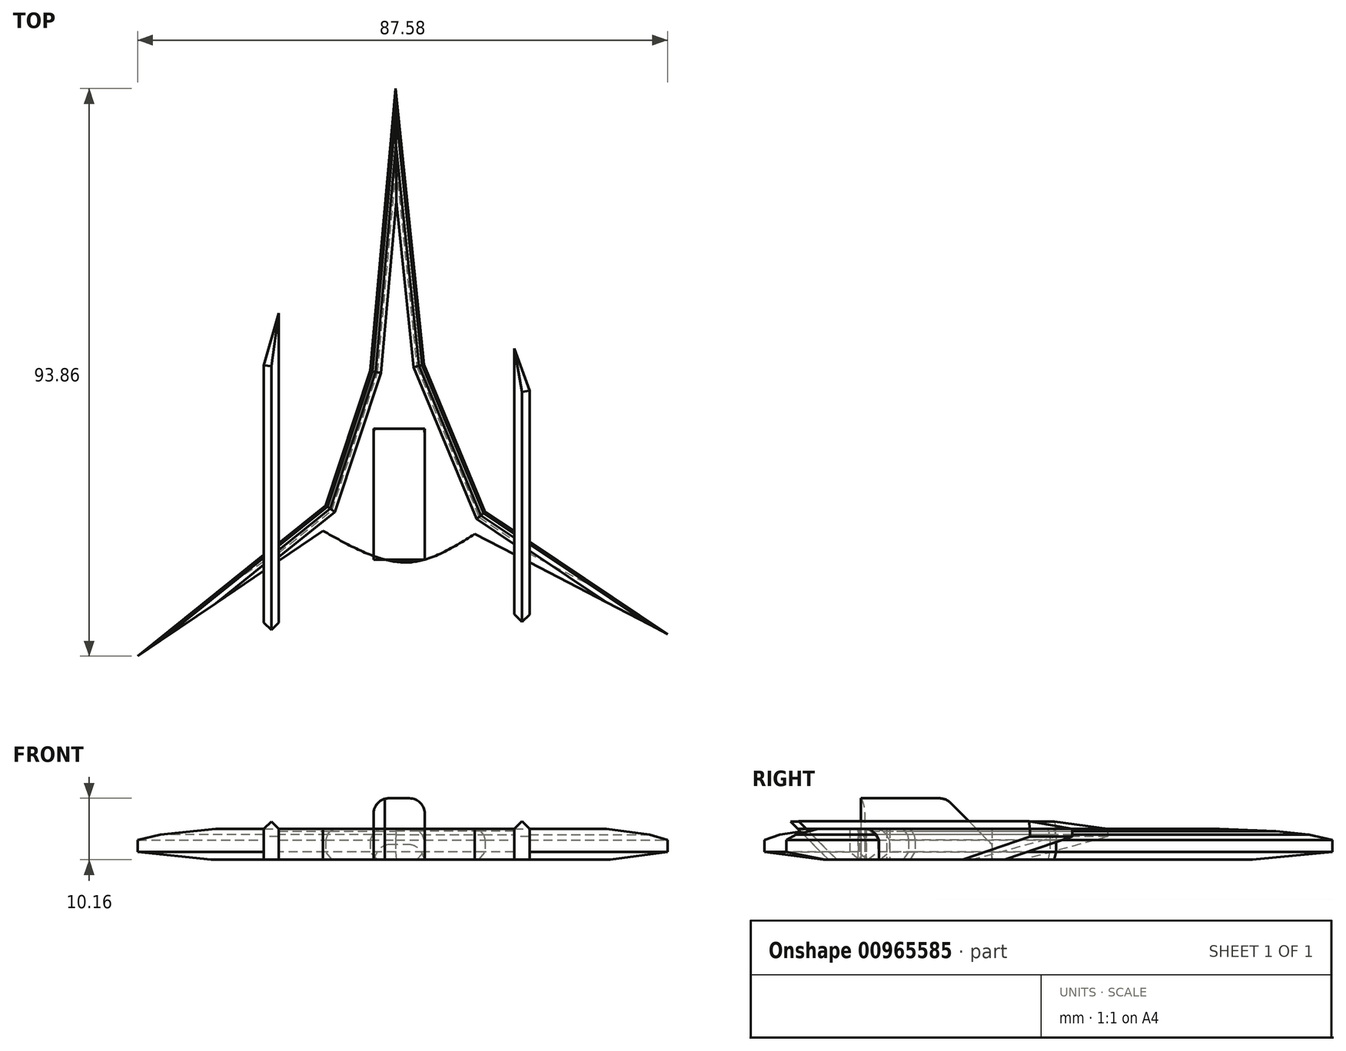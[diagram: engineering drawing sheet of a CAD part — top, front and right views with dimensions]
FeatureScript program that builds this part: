
annotation { "Feature Type Name" : "Feature", "Feature Type Description" : "" }
export const myFeature = defineFeature(function(context is Context, id is Id, definition is map)
    precondition{}
    {
        {
            var Q0;
            Q0=qCreatedBy(makeId("Top.planeOp"),FACE);
            var sketch = newSketch(context, id + "F0", { "sketchPlane" : qUnion([Q0])});
            skLineSegment(sketch, "E0", {"start": v(-29.34, 58.5) * mm, "end": v(-24.64, 12.89) * mm});
            skLineSegment(sketch, "E1", {"start": v(-29.34, 58.5) * mm, "end": v(-33.57, 11.83) * mm});
            skLineSegment(sketch, "E2", {"start": v(-33.57, 11.83) * mm, "end": v(-42.08, -13.88) * mm});
            skLineSegment(sketch, "E3", {"start": v(-24.64, 12.89) * mm, "end": v(-14.54, -11.5) * mm});
            skLineSegment(sketch, "E4", {"start": v(-40.93, -10.42) * mm, "end": v(-72, -35.35) * mm});
            skLineSegment(sketch, "E5", {"start": v(-14.54, -11.5) * mm, "end": v(15.58, -31.7) * mm});
            skLineSegment(sketch, "E6", {"start": v(-72, -35.35) * mm, "end": v(-41.35, -14.63) * mm});
            skLineSegment(sketch, "E7", {"start": v(15.58, -31.7) * mm, "end": v(-16.28, -15.15) * mm});
            skFitSpline(sketch, "E8", {"points": [v(-16.28, -15.15) * mm, v(-27.6, -19.85) * mm, v(-41.35, -14.63) * mm], "startDerivative": vector(-23.1, -14.59) * mm, "endDerivative": vector(-26.99, 15.18) * mm});
            skLineSegment(sketch, "E9.bottom", {"start": v(-33, 2.26) * mm, "end": v(-24.55, 2.26) * mm});
            skLineSegment(sketch, "E9.top", {"start": v(-33, -19.38) * mm, "end": v(-24.55, -19.38) * mm});
            skLineSegment(sketch, "E9.left", {"start": v(-33, 2.26) * mm, "end": v(-33, -19.38) * mm});
            skLineSegment(sketch, "E9.right", {"start": v(-24.55, 2.26) * mm, "end": v(-24.55, -19.38) * mm});
            skLineSegment(sketch, "E10", {"start": v(-51.12, 12.75) * mm, "end": v(-51.12, -32.34) * mm});
            skLineSegment(sketch, "E11", {"start": v(-51.12, -32.34) * mm, "end": v(-48.68, -32.36) * mm});
            skLineSegment(sketch, "E12", {"start": v(-48.68, -32.36) * mm, "end": v(-48.68, 21.35) * mm});
            skLineSegment(sketch, "E13", {"start": v(-48.68, 21.35) * mm, "end": v(-51.12, 12.75) * mm});
            skLineSegment(sketch, "E14", {"start": v(-9.77, 15.52) * mm, "end": v(-9.77, -30.95) * mm});
            skLineSegment(sketch, "E15", {"start": v(-7.24, -30.98) * mm, "end": v(-7.24, 8.56) * mm});
            skLineSegment(sketch, "E16", {"start": v(-7.24, 8.56) * mm, "end": v(-9.77, 15.52) * mm});
            skLineSegment(sketch, "E17", {"start": v(-7.24, -30.98) * mm, "end": v(-9.77, -30.95) * mm});
            skSolve(sketch);
        }
        {
            var Q0;
            Q0=makeQuery(id+"F0.imprint","IMPRINT",FACE,{"disambiguationData":[TD([[makeQuery(id+"F0.imprint","IMPRINT",EDGE,{"derivedFrom":sQuery(id+"F0.wireOp",EDGE,"E0")}),-1.0]])]});
            var Q1;
            {var subQ0=sQuery(id+"F0.wireOp",EDGE,"E9.top");var subQ1=sQuery(id+"F0.wireOp",EDGE,"E8");var subQ3=makeQuery(id+"F0.imprint","INTERSECT",VERTEX,{"derivedFrom":[subQ1,subQ0]});Q1=makeQuery(id+"F0.imprint","IMPRINT",FACE,{"disambiguationData":[TD([[makeQuery(id+"F0.imprint","IMPRINT",EDGE,{"disambiguationData":[TD([[subQ3,1.0]])],"derivedFrom":subQ1}),-1.0]])]});}
            var Q2;
            {var subQ0=sQuery(id+"F0.wireOp",EDGE,"E9.top");var subQ1=sQuery(id+"F0.wireOp",EDGE,"E8");var subQ2=makeQuery(id+"F0.imprint","INTERSECT",VERTEX,{"derivedFrom":[subQ1,subQ0]});Q2=makeQuery(id+"F0.imprint","IMPRINT",FACE,{"disambiguationData":[TD([[makeQuery(id+"F0.imprint","IMPRINT",EDGE,{"disambiguationData":[TD([[subQ2,-1.0]])],"derivedFrom":subQ1}),1.0]])]});}
            var Q3;
            {var subQ0=sQuery(id+"F0.wireOp",EDGE,"E6");var subQ1=sQuery(id+"F0.wireOp",EDGE,"E4");var subQ2=makeQuery(id+"F0.imprint","INTERSECT",VERTEX,{"derivedFrom":[subQ1,subQ0]});Q3=makeQuery(id+"F0.imprint","IMPRINT",FACE,{"disambiguationData":[TD([[makeQuery(id+"F0.imprint","IMPRINT",EDGE,{"disambiguationData":[TD([[subQ2,1.0]])],"derivedFrom":subQ1}),1.0]])]});}
            var Q4;
            {var subQ0=sQuery(id+"F0.wireOp",EDGE,"E7");var subQ1=sQuery(id+"F0.wireOp",EDGE,"E5");var subQ2=makeQuery(id+"F0.imprint","INTERSECT",VERTEX,{"derivedFrom":[subQ1,subQ0]});Q4=makeQuery(id+"F0.imprint","IMPRINT",FACE,{"disambiguationData":[TD([[makeQuery(id+"F0.imprint","IMPRINT",EDGE,{"disambiguationData":[TD([[subQ2,1.0]])],"derivedFrom":subQ1}),-1.0]])]});}
            extrude(context, id + "F1", {"entities" : qUnion([Q0, Q1, Q2, Q3, Q4]), "depth" : 5.08 * mm, "offsetDistance" : 25.4 * mm});
        }
        {
            var Q0;
            Q0=makeQuery(id+"F1.opExtrude","CAP_EDGE",EDGE,{"disambiguationData":[OSD([sQuery(id+"F0.wireOp",EDGE,"E0")])],"isStart":false});
            var Q1;
            Q1=makeQuery(id+"F1.opExtrude","CAP_EDGE",EDGE,{"disambiguationData":[OSD([sQuery(id+"F0.wireOp",EDGE,"E1")])],"isStart":false});
            var Q2;
            Q2=makeQuery(id+"F1.opExtrude","CAP_EDGE",EDGE,{"disambiguationData":[OSD([sQuery(id+"F0.wireOp",EDGE,"E2")])],"isStart":false});
            var Q3;
            Q3=makeQuery(id+"F1.opExtrude","CAP_EDGE",EDGE,{"disambiguationData":[OSD([sQuery(id+"F0.wireOp",EDGE,"E3")])],"isStart":false});
            var Q4;
            {var subQ0=sQuery(id+"F0.wireOp",EDGE,"E4");Q4=makeQuery(id+"F1.opExtrude","CAP_EDGE",EDGE,{"disambiguationData":[OSD([subQ0]),TDD([makeQuery(id+"F0.imprint","IMPRINT",EDGE,{"disambiguationData":[TD([[makeQuery(id+"F0.imprint","INTERSECT",VERTEX,{"derivedFrom":[subQ0,sQuery(id+"F0.wireOp",EDGE,"E6")]}),1.0]])],"derivedFrom":subQ0})])],"isStart":false});}
            var Q5;
            {var subQ0=sQuery(id+"F0.wireOp",EDGE,"E5");Q5=makeQuery(id+"F1.opExtrude","CAP_EDGE",EDGE,{"disambiguationData":[OSD([subQ0]),TDD([makeQuery(id+"F0.imprint","IMPRINT",EDGE,{"disambiguationData":[TD([[makeQuery(id+"F0.imprint","INTERSECT",VERTEX,{"derivedFrom":[subQ0,sQuery(id+"F0.wireOp",EDGE,"E7")]}),1.0]])],"derivedFrom":subQ0})])],"isStart":false});}
            var Q6;
            {var subQ0=sQuery(id+"F0.wireOp",EDGE,"E4");Q6=makeQuery(id+"F1.opExtrude","CAP_EDGE",EDGE,{"disambiguationData":[OSD([subQ0]),TDD([makeQuery(id+"F0.imprint","IMPRINT",EDGE,{"disambiguationData":[TD([[makeQuery(id+"F0.imprint","INTERSECT",VERTEX,{"derivedFrom":[sQuery(id+"F0.wireOp",EDGE,"E2"),subQ0]}),-1.0]])],"derivedFrom":subQ0})])],"isStart":false});}
            var Q7;
            {var subQ0=sQuery(id+"F0.wireOp",EDGE,"E5");Q7=makeQuery(id+"F1.opExtrude","CAP_EDGE",EDGE,{"disambiguationData":[OSD([subQ0]),TDD([makeQuery(id+"F0.imprint","IMPRINT",EDGE,{"disambiguationData":[TD([[makeQuery(id+"F0.imprint","INTERSECT",VERTEX,{"derivedFrom":[sQuery(id+"F0.wireOp",EDGE,"E3"),subQ0]}),-1.0]])],"derivedFrom":subQ0})])],"isStart":false});}
            var Q8;
            {var subQ0=sQuery(id+"F0.wireOp",EDGE,"E6");Q8=makeQuery(id+"F1.opExtrude","CAP_EDGE",EDGE,{"disambiguationData":[OSD([subQ0]),TDD([makeQuery(id+"F0.imprint","IMPRINT",EDGE,{"disambiguationData":[TD([[makeQuery(id+"F0.imprint","INTERSECT",VERTEX,{"derivedFrom":[sQuery(id+"F0.wireOp",EDGE,"E4"),subQ0]}),-1.0]])],"derivedFrom":subQ0})])],"isStart":true});}
            var Q9;
            {var subQ0=sQuery(id+"F0.wireOp",EDGE,"E7");Q9=makeQuery(id+"F1.opExtrude","CAP_EDGE",EDGE,{"disambiguationData":[OSD([subQ0]),TDD([makeQuery(id+"F0.imprint","IMPRINT",EDGE,{"disambiguationData":[TD([[makeQuery(id+"F0.imprint","INTERSECT",VERTEX,{"derivedFrom":[sQuery(id+"F0.wireOp",EDGE,"E5"),subQ0]}),-1.0]])],"derivedFrom":subQ0})])],"isStart":true});}
            var Q10;
            Q10=makeQuery(id+"F1.opExtrude","CAP_EDGE",EDGE,{"disambiguationData":[OSD([sQuery(id+"F0.wireOp",EDGE,"E1")])],"isStart":true});
            var Q11;
            Q11=makeQuery(id+"F1.opExtrude","CAP_EDGE",EDGE,{"disambiguationData":[OSD([sQuery(id+"F0.wireOp",EDGE,"E0")])],"isStart":true});
            var Q12;
            Q12=makeQuery(id+"F1.opExtrude","CAP_EDGE",EDGE,{"disambiguationData":[OSD([sQuery(id+"F0.wireOp",EDGE,"E2")])],"isStart":true});
            var Q13;
            Q13=makeQuery(id+"F1.opExtrude","CAP_EDGE",EDGE,{"disambiguationData":[OSD([sQuery(id+"F0.wireOp",EDGE,"E3")])],"isStart":true});
            var Q14;
            {var subQ0=sQuery(id+"F0.wireOp",EDGE,"E4");Q14=makeQuery(id+"F1.opExtrude","CAP_EDGE",EDGE,{"disambiguationData":[OSD([subQ0]),TDD([makeQuery(id+"F0.imprint","IMPRINT",EDGE,{"disambiguationData":[TD([[makeQuery(id+"F0.imprint","INTERSECT",VERTEX,{"derivedFrom":[sQuery(id+"F0.wireOp",EDGE,"E2"),subQ0]}),-1.0]])],"derivedFrom":subQ0})])],"isStart":true});}
            var Q15;
            {var subQ0=sQuery(id+"F0.wireOp",EDGE,"E5");Q15=makeQuery(id+"F1.opExtrude","CAP_EDGE",EDGE,{"disambiguationData":[OSD([subQ0]),TDD([makeQuery(id+"F0.imprint","IMPRINT",EDGE,{"disambiguationData":[TD([[makeQuery(id+"F0.imprint","INTERSECT",VERTEX,{"derivedFrom":[sQuery(id+"F0.wireOp",EDGE,"E3"),subQ0]}),-1.0]])],"derivedFrom":subQ0})])],"isStart":true});}
            chamfer(context, id + "F2", {"entities" : qUnion([Q0, Q1, Q2, Q3, Q4, Q5, Q6, Q7, Q8, Q9, Q10, Q11, Q12, Q13, Q14, Q15]), "width" : 1.27 * mm, "tangentPropagation" : true});
        }
        {
            var Q0;
            {var subQ4=sQuery(id+"F0.wireOp",EDGE,"E9.bottom");Q0=makeQuery(id+"F0.imprint","IMPRINT",FACE,{"disambiguationData":[TD([[makeQuery(id+"F0.imprint","IMPRINT",EDGE,{"derivedFrom":subQ4}),-1.0]])]});}
            extrude(context, id + "F3", {"entities" : qUnion([Q0]), "depth" : 10.16 * mm, "offsetDistance" : 25.4 * mm});
        }
        {
            var Q0;
            Q0=makeQuery(id+"F3.opExtrude","CAP_EDGE",EDGE,{"disambiguationData":[OSD([sQuery(id+"F0.wireOp",EDGE,"E9.bottom")])],"isStart":false});
            chamfer(context, id + "F4", {"entities" : qUnion([Q0]), "width" : 7.62 * mm, "tangentPropagation" : true});
        }
        {
            var Q0;
            Q0=makeQuery(id+"F3.opExtrude","CAP_EDGE",EDGE,{"disambiguationData":[OSD([sQuery(id+"F0.wireOp",EDGE,"E9.left")])],"isStart":false});
            var Q1;
            Q1=makeQuery(id+"F3.opExtrude","CAP_EDGE",EDGE,{"disambiguationData":[OSD([sQuery(id+"F0.wireOp",EDGE,"E9.right")])],"isStart":false});
            var Q2;
            {var subQ0=sQuery(id+"F0.wireOp",EDGE,"E9.bottom");Q2=makeQuery(id+"F4.opChamfer","BLEND_EDGE",EDGE,{"blendedFrom":[makeQuery(id+"F3.opExtrude","CAP_EDGE",EDGE,{"disambiguationData":[OSD([subQ0])],"isStart":false}),makeQuery(id+"F3.opExtrude","CAP_FACE",FACE,{"disambiguationData":[OSD([sQuery(id+"F0.wireOp",EDGE,"E8"),subQ0,sQuery(id+"F0.wireOp",EDGE,"E9.top"),sQuery(id+"F0.wireOp",EDGE,"E9.left"),sQuery(id+"F0.wireOp",EDGE,"E9.right")])],"isStart":false})],"blendedInto":[makeQuery(id+"F3.opExtrude","CAP_FACE",FACE,{"disambiguationData":[OSD([sQuery(id+"F0.wireOp",EDGE,"E8"),subQ0,sQuery(id+"F0.wireOp",EDGE,"E9.top"),sQuery(id+"F0.wireOp",EDGE,"E9.left"),sQuery(id+"F0.wireOp",EDGE,"E9.right")])],"isStart":false})]});}
            var Q3;
            Q3=makeQuery(id+"F4.opChamfer","BLEND_EDGE",EDGE,{"blendedFrom":[makeQuery(id+"F3.opExtrude","CAP_EDGE",EDGE,{"disambiguationData":[OSD([sQuery(id+"F0.wireOp",EDGE,"E9.bottom")])],"isStart":false}),makeQuery(id+"F3.opExtrude","SWEPT_FACE",FACE,{"disambiguationData":[OSD([sQuery(id+"F0.wireOp",EDGE,"E9.right")])]})],"blendedInto":[makeQuery(id+"F3.opExtrude","SWEPT_FACE",FACE,{"disambiguationData":[OSD([sQuery(id+"F0.wireOp",EDGE,"E9.right")])]})]});
            var Q4;
            Q4=makeQuery(id+"F4.opChamfer","BLEND_EDGE",EDGE,{"blendedFrom":[makeQuery(id+"F3.opExtrude","CAP_EDGE",EDGE,{"disambiguationData":[OSD([sQuery(id+"F0.wireOp",EDGE,"E9.bottom")])],"isStart":false}),makeQuery(id+"F3.opExtrude","SWEPT_FACE",FACE,{"disambiguationData":[OSD([sQuery(id+"F0.wireOp",EDGE,"E9.left")])]})],"blendedInto":[makeQuery(id+"F3.opExtrude","SWEPT_FACE",FACE,{"disambiguationData":[OSD([sQuery(id+"F0.wireOp",EDGE,"E9.left")])]})]});
            fillet(context, id + "F5", {"entities" : qUnion([Q0, Q1, Q2, Q3, Q4]), "radius" : 2.54 * mm, "tangentPropagation" : true, "allowEdgeOverflow" : false});
        }
        {
            var Q0;
            {var subQ5=sQuery(id+"F0.wireOp",EDGE,"E13");Q0=makeQuery(id+"F0.imprint","IMPRINT",FACE,{"disambiguationData":[TD([[makeQuery(id+"F0.imprint","IMPRINT",EDGE,{"derivedFrom":subQ5}),1.0]])]});}
            var Q1;
            {var subQ0=sQuery(id+"F0.wireOp",EDGE,"E12");var subQ1=sQuery(id+"F0.wireOp",EDGE,"E4");var subQ2=makeQuery(id+"F0.imprint","INTERSECT",VERTEX,{"derivedFrom":[subQ1,subQ0]});Q1=makeQuery(id+"F0.imprint","IMPRINT",FACE,{"disambiguationData":[TD([[makeQuery(id+"F0.imprint","IMPRINT",EDGE,{"disambiguationData":[TD([[subQ2,-1.0]])],"derivedFrom":subQ1}),1.0]])]});}
            var Q2;
            {var subQ5=sQuery(id+"F0.wireOp",EDGE,"E11");Q2=makeQuery(id+"F0.imprint","IMPRINT",FACE,{"disambiguationData":[TD([[makeQuery(id+"F0.imprint","IMPRINT",EDGE,{"derivedFrom":subQ5}),1.0]])]});}
            var Q3;
            {var subQ5=sQuery(id+"F0.wireOp",EDGE,"SbuKVpWi-p680-YLej-fJ7i-d89EKV01Oxsp");Q3=makeQuery(id+"F0.imprint","IMPRINT",FACE,{"disambiguationData":[TD([[makeQuery(id+"F0.imprint","IMPRINT",EDGE,{"derivedFrom":subQ5}),1.0]])]});}
            var Q4;
            {var subQ0=sQuery(id+"F0.wireOp",EDGE,"E14");var subQ1=sQuery(id+"F0.wireOp",EDGE,"E5");var subQ2=makeQuery(id+"F0.imprint","INTERSECT",VERTEX,{"derivedFrom":[subQ1,subQ0]});Q4=makeQuery(id+"F0.imprint","IMPRINT",FACE,{"disambiguationData":[TD([[makeQuery(id+"F0.imprint","IMPRINT",EDGE,{"disambiguationData":[TD([[subQ2,-1.0]])],"derivedFrom":subQ1}),-1.0]])]});}
            var Q5;
            {var subQ5=sQuery(id+"F0.wireOp",EDGE,"E16");Q5=makeQuery(id+"F0.imprint","IMPRINT",FACE,{"disambiguationData":[TD([[makeQuery(id+"F0.imprint","IMPRINT",EDGE,{"derivedFrom":subQ5}),1.0]])]});}
            var Q6;
            {var subQ5=sQuery(id+"F0.wireOp",EDGE,"E17");Q6=makeQuery(id+"F0.imprint","IMPRINT",FACE,{"disambiguationData":[TD([[makeQuery(id+"F0.imprint","IMPRINT",EDGE,{"derivedFrom":subQ5}),-1.0]])]});}
            extrude(context, id + "F6", {"entities" : qUnion([Q0, Q1, Q2, Q3, Q4, Q5, Q6]), "operationType" : NewBodyOperationType.ADD, "depth" : 6.35 * mm, "offsetDistance" : 25.4 * mm});
        }
        {
            var Q0;
            Q0=makeQuery(id+"F6.opExtrude","CAP_EDGE",EDGE,{"disambiguationData":[OSD([sQuery(id+"F0.wireOp",EDGE,"E13")])],"isStart":false});
            var Q1;
            Q1=makeQuery(id+"F6.opExtrude","CAP_EDGE",EDGE,{"disambiguationData":[OSD([sQuery(id+"F0.wireOp",EDGE,"E10")])],"isStart":false});
            var Q2;
            Q2=makeQuery(id+"F6.opExtrude","CAP_EDGE",EDGE,{"disambiguationData":[OSD([sQuery(id+"F0.wireOp",EDGE,"E15")])],"isStart":false});
            var Q3;
            Q3=makeQuery(id+"F6.opExtrude","CAP_EDGE",EDGE,{"disambiguationData":[OSD([sQuery(id+"F0.wireOp",EDGE,"E16")])],"isStart":false});
            chamfer(context, id + "F7", {"entities" : qUnion([Q0, Q1, Q2, Q3]), "width" : 1.27 * mm, "tangentPropagation" : true});
        }
        {
            var Q0;
            Q0=makeQuery(id+"F6.opExtrude","CAP_EDGE",EDGE,{"disambiguationData":[OSD([sQuery(id+"F0.wireOp",EDGE,"E11")])],"isStart":true});
            var Q1;
            Q1=makeQuery(id+"F6.opExtrude","CAP_EDGE",EDGE,{"disambiguationData":[OSD([sQuery(id+"F0.wireOp",EDGE,"E17")])],"isStart":true});
            chamfer(context, id + "F8", {"entities" : qUnion([Q0, Q1]), "width" : 7.62 * mm, "tangentPropagation" : true});
        }
        {
            var Q0;
            Q0=makeQuery(id+"F6.opExtrude","CAP_EDGE",EDGE,{"disambiguationData":[OSD([sQuery(id+"F0.wireOp",EDGE,"E13")])],"isStart":true});
            var Q1;
            Q1=makeQuery(id+"F6.opExtrude","CAP_EDGE",EDGE,{"disambiguationData":[OSD([sQuery(id+"F0.wireOp",EDGE,"E16")])],"isStart":true});
            chamfer(context, id + "F9", {"entities" : qUnion([Q0, Q1]), "width" : 3.8 * mm, "tangentPropagation" : true});
        }
        {
            var Q0;
            Q0=makeQuery(id+"F6.opExtrude","CAP_EDGE",EDGE,{"disambiguationData":[OSD([sQuery(id+"F0.wireOp",EDGE,"E12")])],"isStart":false});
            var Q1;
            Q1=makeQuery(id+"F6.opExtrude","CAP_EDGE",EDGE,{"disambiguationData":[OSD([sQuery(id+"F0.wireOp",EDGE,"E14")])],"isStart":false});
            var Q2;
            {var subQ0=sQuery(id+"F0.wireOp",EDGE,"E1");Q2=makeQuery(id+"F2.opChamfer","BLEND_EDGE",EDGE,{"blendedFrom":[makeQuery(id+"F1.opExtrude","CAP_EDGE",EDGE,{"disambiguationData":[OSD([subQ0])],"isStart":false}),makeQuery(id+"F1.opExtrude","CAP_FACE",FACE,{"disambiguationData":[OSD([sQuery(id+"F0.wireOp",EDGE,"E0"),subQ0,sQuery(id+"F0.wireOp",EDGE,"E2"),sQuery(id+"F0.wireOp",EDGE,"E3"),sQuery(id+"F0.wireOp",EDGE,"E4"),sQuery(id+"F0.wireOp",EDGE,"E5"),sQuery(id+"F0.wireOp",EDGE,"E6"),sQuery(id+"F0.wireOp",EDGE,"E7"),sQuery(id+"F0.wireOp",EDGE,"E8"),sQuery(id+"F0.wireOp",EDGE,"E9.bottom"),sQuery(id+"F0.wireOp",EDGE,"E9.left"),sQuery(id+"F0.wireOp",EDGE,"E9.right"),sQuery(id+"F0.wireOp",EDGE,"E12"),sQuery(id+"F0.wireOp",EDGE,"E14")])],"isStart":false})],"blendedInto":[makeQuery(id+"F1.opExtrude","CAP_FACE",FACE,{"disambiguationData":[OSD([sQuery(id+"F0.wireOp",EDGE,"E0"),subQ0,sQuery(id+"F0.wireOp",EDGE,"E2"),sQuery(id+"F0.wireOp",EDGE,"E3"),sQuery(id+"F0.wireOp",EDGE,"E4"),sQuery(id+"F0.wireOp",EDGE,"E5"),sQuery(id+"F0.wireOp",EDGE,"E6"),sQuery(id+"F0.wireOp",EDGE,"E7"),sQuery(id+"F0.wireOp",EDGE,"E8"),sQuery(id+"F0.wireOp",EDGE,"E9.bottom"),sQuery(id+"F0.wireOp",EDGE,"E9.left"),sQuery(id+"F0.wireOp",EDGE,"E9.right"),sQuery(id+"F0.wireOp",EDGE,"E12"),sQuery(id+"F0.wireOp",EDGE,"E14")])],"isStart":false})]});}
            var Q3;
            {var subQ0=sQuery(id+"F0.wireOp",EDGE,"E0");Q3=makeQuery(id+"F2.opChamfer","BLEND_EDGE",EDGE,{"blendedFrom":[makeQuery(id+"F1.opExtrude","CAP_EDGE",EDGE,{"disambiguationData":[OSD([subQ0])],"isStart":false}),makeQuery(id+"F1.opExtrude","CAP_FACE",FACE,{"disambiguationData":[OSD([subQ0,sQuery(id+"F0.wireOp",EDGE,"E1"),sQuery(id+"F0.wireOp",EDGE,"E2"),sQuery(id+"F0.wireOp",EDGE,"E3"),sQuery(id+"F0.wireOp",EDGE,"E4"),sQuery(id+"F0.wireOp",EDGE,"E5"),sQuery(id+"F0.wireOp",EDGE,"E6"),sQuery(id+"F0.wireOp",EDGE,"E7"),sQuery(id+"F0.wireOp",EDGE,"E8"),sQuery(id+"F0.wireOp",EDGE,"E9.bottom"),sQuery(id+"F0.wireOp",EDGE,"E9.left"),sQuery(id+"F0.wireOp",EDGE,"E9.right"),sQuery(id+"F0.wireOp",EDGE,"E12"),sQuery(id+"F0.wireOp",EDGE,"E14")])],"isStart":false})],"blendedInto":[makeQuery(id+"F1.opExtrude","CAP_FACE",FACE,{"disambiguationData":[OSD([subQ0,sQuery(id+"F0.wireOp",EDGE,"E1"),sQuery(id+"F0.wireOp",EDGE,"E2"),sQuery(id+"F0.wireOp",EDGE,"E3"),sQuery(id+"F0.wireOp",EDGE,"E4"),sQuery(id+"F0.wireOp",EDGE,"E5"),sQuery(id+"F0.wireOp",EDGE,"E6"),sQuery(id+"F0.wireOp",EDGE,"E7"),sQuery(id+"F0.wireOp",EDGE,"E8"),sQuery(id+"F0.wireOp",EDGE,"E9.bottom"),sQuery(id+"F0.wireOp",EDGE,"E9.left"),sQuery(id+"F0.wireOp",EDGE,"E9.right"),sQuery(id+"F0.wireOp",EDGE,"E12"),sQuery(id+"F0.wireOp",EDGE,"E14")])],"isStart":false})]});}
            var Q4;
            {var subQ0=sQuery(id+"F0.wireOp",EDGE,"E2");Q4=makeQuery(id+"F2.opChamfer","BLEND_EDGE",EDGE,{"blendedFrom":[makeQuery(id+"F1.opExtrude","CAP_EDGE",EDGE,{"disambiguationData":[OSD([subQ0])],"isStart":false}),makeQuery(id+"F1.opExtrude","CAP_FACE",FACE,{"disambiguationData":[OSD([sQuery(id+"F0.wireOp",EDGE,"E0"),sQuery(id+"F0.wireOp",EDGE,"E1"),subQ0,sQuery(id+"F0.wireOp",EDGE,"E3"),sQuery(id+"F0.wireOp",EDGE,"E4"),sQuery(id+"F0.wireOp",EDGE,"E5"),sQuery(id+"F0.wireOp",EDGE,"E6"),sQuery(id+"F0.wireOp",EDGE,"E7"),sQuery(id+"F0.wireOp",EDGE,"E8"),sQuery(id+"F0.wireOp",EDGE,"E9.bottom"),sQuery(id+"F0.wireOp",EDGE,"E9.left"),sQuery(id+"F0.wireOp",EDGE,"E9.right"),sQuery(id+"F0.wireOp",EDGE,"E12"),sQuery(id+"F0.wireOp",EDGE,"E14")])],"isStart":false})],"blendedInto":[makeQuery(id+"F1.opExtrude","CAP_FACE",FACE,{"disambiguationData":[OSD([sQuery(id+"F0.wireOp",EDGE,"E0"),sQuery(id+"F0.wireOp",EDGE,"E1"),subQ0,sQuery(id+"F0.wireOp",EDGE,"E3"),sQuery(id+"F0.wireOp",EDGE,"E4"),sQuery(id+"F0.wireOp",EDGE,"E5"),sQuery(id+"F0.wireOp",EDGE,"E6"),sQuery(id+"F0.wireOp",EDGE,"E7"),sQuery(id+"F0.wireOp",EDGE,"E8"),sQuery(id+"F0.wireOp",EDGE,"E9.bottom"),sQuery(id+"F0.wireOp",EDGE,"E9.left"),sQuery(id+"F0.wireOp",EDGE,"E9.right"),sQuery(id+"F0.wireOp",EDGE,"E12"),sQuery(id+"F0.wireOp",EDGE,"E14")])],"isStart":false})]});}
            var Q5;
            {var subQ0=sQuery(id+"F0.wireOp",EDGE,"E3");Q5=makeQuery(id+"F2.opChamfer","BLEND_EDGE",EDGE,{"blendedFrom":[makeQuery(id+"F1.opExtrude","CAP_EDGE",EDGE,{"disambiguationData":[OSD([subQ0])],"isStart":false}),makeQuery(id+"F1.opExtrude","CAP_FACE",FACE,{"disambiguationData":[OSD([sQuery(id+"F0.wireOp",EDGE,"E0"),sQuery(id+"F0.wireOp",EDGE,"E1"),sQuery(id+"F0.wireOp",EDGE,"E2"),subQ0,sQuery(id+"F0.wireOp",EDGE,"E4"),sQuery(id+"F0.wireOp",EDGE,"E5"),sQuery(id+"F0.wireOp",EDGE,"E6"),sQuery(id+"F0.wireOp",EDGE,"E7"),sQuery(id+"F0.wireOp",EDGE,"E8"),sQuery(id+"F0.wireOp",EDGE,"E9.bottom"),sQuery(id+"F0.wireOp",EDGE,"E9.left"),sQuery(id+"F0.wireOp",EDGE,"E9.right"),sQuery(id+"F0.wireOp",EDGE,"E12"),sQuery(id+"F0.wireOp",EDGE,"E14")])],"isStart":false})],"blendedInto":[makeQuery(id+"F1.opExtrude","CAP_FACE",FACE,{"disambiguationData":[OSD([sQuery(id+"F0.wireOp",EDGE,"E0"),sQuery(id+"F0.wireOp",EDGE,"E1"),sQuery(id+"F0.wireOp",EDGE,"E2"),subQ0,sQuery(id+"F0.wireOp",EDGE,"E4"),sQuery(id+"F0.wireOp",EDGE,"E5"),sQuery(id+"F0.wireOp",EDGE,"E6"),sQuery(id+"F0.wireOp",EDGE,"E7"),sQuery(id+"F0.wireOp",EDGE,"E8"),sQuery(id+"F0.wireOp",EDGE,"E9.bottom"),sQuery(id+"F0.wireOp",EDGE,"E9.left"),sQuery(id+"F0.wireOp",EDGE,"E9.right"),sQuery(id+"F0.wireOp",EDGE,"E12"),sQuery(id+"F0.wireOp",EDGE,"E14")])],"isStart":false})]});}
            var Q6;
            {var subQ0=sQuery(id+"F0.wireOp",EDGE,"E3");Q6=makeQuery(id+"F2.opChamfer","BLEND_EDGE",EDGE,{"blendedFrom":[makeQuery(id+"F1.opExtrude","CAP_EDGE",EDGE,{"disambiguationData":[OSD([subQ0])],"isStart":false}),makeQuery(id+"F1.opExtrude","SWEPT_FACE",FACE,{"disambiguationData":[OSD([subQ0])]})],"blendedInto":[makeQuery(id+"F1.opExtrude","SWEPT_FACE",FACE,{"disambiguationData":[OSD([subQ0])]})]});}
            var Q7;
            {var subQ0=sQuery(id+"F0.wireOp",EDGE,"E0");Q7=makeQuery(id+"F2.opChamfer","BLEND_EDGE",EDGE,{"blendedFrom":[makeQuery(id+"F1.opExtrude","CAP_EDGE",EDGE,{"disambiguationData":[OSD([subQ0])],"isStart":false}),makeQuery(id+"F1.opExtrude","SWEPT_FACE",FACE,{"disambiguationData":[OSD([subQ0])]})],"blendedInto":[makeQuery(id+"F1.opExtrude","SWEPT_FACE",FACE,{"disambiguationData":[OSD([subQ0])]})]});}
            var Q8;
            {var subQ0=sQuery(id+"F0.wireOp",EDGE,"E1");Q8=makeQuery(id+"F2.opChamfer","BLEND_EDGE",EDGE,{"blendedFrom":[makeQuery(id+"F1.opExtrude","CAP_EDGE",EDGE,{"disambiguationData":[OSD([subQ0])],"isStart":false}),makeQuery(id+"F1.opExtrude","SWEPT_FACE",FACE,{"disambiguationData":[OSD([subQ0])]})],"blendedInto":[makeQuery(id+"F1.opExtrude","SWEPT_FACE",FACE,{"disambiguationData":[OSD([subQ0])]})]});}
            var Q9;
            {var subQ0=sQuery(id+"F0.wireOp",EDGE,"E2");Q9=makeQuery(id+"F2.opChamfer","BLEND_EDGE",EDGE,{"blendedFrom":[makeQuery(id+"F1.opExtrude","CAP_EDGE",EDGE,{"disambiguationData":[OSD([subQ0])],"isStart":false}),makeQuery(id+"F1.opExtrude","SWEPT_FACE",FACE,{"disambiguationData":[OSD([subQ0])]})],"blendedInto":[makeQuery(id+"F1.opExtrude","SWEPT_FACE",FACE,{"disambiguationData":[OSD([subQ0])]})]});}
            var Q10;
            {var subQ0=sQuery(id+"F0.wireOp",EDGE,"E5");var subQ1=makeQuery(id+"F0.imprint","IMPRINT",EDGE,{"disambiguationData":[TD([[makeQuery(id+"F0.imprint","INTERSECT",VERTEX,{"derivedFrom":[subQ0,sQuery(id+"F0.wireOp",EDGE,"E7")]}),1.0]])],"derivedFrom":subQ0});Q10=makeQuery(id+"F2.opChamfer","BLEND_EDGE",EDGE,{"blendedFrom":[makeQuery(id+"F1.opExtrude","CAP_EDGE",EDGE,{"disambiguationData":[OSD([subQ0]),TDD([subQ1])],"isStart":false}),makeQuery(id+"F1.opExtrude","SWEPT_FACE",FACE,{"disambiguationData":[OSD([subQ0]),TDD([subQ1])]})],"blendedInto":[makeQuery(id+"F1.opExtrude","SWEPT_FACE",FACE,{"disambiguationData":[OSD([subQ0]),TDD([subQ1])]})]});}
            var Q11;
            {var subQ0=sQuery(id+"F0.wireOp",EDGE,"E4");var subQ1=makeQuery(id+"F0.imprint","IMPRINT",EDGE,{"disambiguationData":[TD([[makeQuery(id+"F0.imprint","INTERSECT",VERTEX,{"derivedFrom":[subQ0,sQuery(id+"F0.wireOp",EDGE,"E6")]}),1.0]])],"derivedFrom":subQ0});Q11=makeQuery(id+"F2.opChamfer","BLEND_EDGE",EDGE,{"blendedFrom":[makeQuery(id+"F1.opExtrude","CAP_EDGE",EDGE,{"disambiguationData":[OSD([subQ0]),TDD([subQ1])],"isStart":false}),makeQuery(id+"F1.opExtrude","SWEPT_FACE",FACE,{"disambiguationData":[OSD([subQ0]),TDD([subQ1])]})],"blendedInto":[makeQuery(id+"F1.opExtrude","SWEPT_FACE",FACE,{"disambiguationData":[OSD([subQ0]),TDD([subQ1])]})]});}
            var Q12;
            {var subQ0=sQuery(id+"F0.wireOp",EDGE,"E4");var subQ1=makeQuery(id+"F0.imprint","IMPRINT",EDGE,{"disambiguationData":[TD([[makeQuery(id+"F0.imprint","INTERSECT",VERTEX,{"derivedFrom":[sQuery(id+"F0.wireOp",EDGE,"E2"),subQ0]}),-1.0]])],"derivedFrom":subQ0});Q12=makeQuery(id+"F2.opChamfer","BLEND_EDGE",EDGE,{"blendedFrom":[makeQuery(id+"F1.opExtrude","CAP_EDGE",EDGE,{"disambiguationData":[OSD([subQ0]),TDD([subQ1])],"isStart":false}),makeQuery(id+"F1.opExtrude","SWEPT_FACE",FACE,{"disambiguationData":[OSD([subQ0]),TDD([subQ1])]})],"blendedInto":[makeQuery(id+"F1.opExtrude","SWEPT_FACE",FACE,{"disambiguationData":[OSD([subQ0]),TDD([subQ1])]})]});}
            var Q13;
            {var subQ0=sQuery(id+"F0.wireOp",EDGE,"E12");var subQ1=sQuery(id+"F0.wireOp",EDGE,"E4");var subQ2=sQuery(id+"F0.wireOp",EDGE,"E2");Q13=makeQuery(id+"F2.opChamfer","BLEND_EDGE",EDGE,{"blendedFrom":[makeQuery(id+"F1.opExtrude","CAP_EDGE",EDGE,{"disambiguationData":[OSD([subQ1]),TDD([makeQuery(id+"F0.imprint","IMPRINT",EDGE,{"disambiguationData":[TD([[makeQuery(id+"F0.imprint","INTERSECT",VERTEX,{"derivedFrom":[subQ2,subQ1]}),-1.0]])],"derivedFrom":subQ1})])],"isStart":false}),makeQuery(id+"F1.opExtrude","CAP_FACE",FACE,{"disambiguationData":[OSD([sQuery(id+"F0.wireOp",EDGE,"E0"),sQuery(id+"F0.wireOp",EDGE,"E1"),subQ2,sQuery(id+"F0.wireOp",EDGE,"E3"),subQ1,sQuery(id+"F0.wireOp",EDGE,"E5"),sQuery(id+"F0.wireOp",EDGE,"E6"),sQuery(id+"F0.wireOp",EDGE,"E7"),sQuery(id+"F0.wireOp",EDGE,"E8"),sQuery(id+"F0.wireOp",EDGE,"E9.bottom"),sQuery(id+"F0.wireOp",EDGE,"E9.left"),sQuery(id+"F0.wireOp",EDGE,"E9.right"),subQ0,sQuery(id+"F0.wireOp",EDGE,"E14")])],"isStart":false})],"blendedInto":[makeQuery(id+"F1.opExtrude","CAP_FACE",FACE,{"disambiguationData":[OSD([sQuery(id+"F0.wireOp",EDGE,"E0"),sQuery(id+"F0.wireOp",EDGE,"E1"),subQ2,sQuery(id+"F0.wireOp",EDGE,"E3"),subQ1,sQuery(id+"F0.wireOp",EDGE,"E5"),sQuery(id+"F0.wireOp",EDGE,"E6"),sQuery(id+"F0.wireOp",EDGE,"E7"),sQuery(id+"F0.wireOp",EDGE,"E8"),sQuery(id+"F0.wireOp",EDGE,"E9.bottom"),sQuery(id+"F0.wireOp",EDGE,"E9.left"),sQuery(id+"F0.wireOp",EDGE,"E9.right"),subQ0,sQuery(id+"F0.wireOp",EDGE,"E14")])],"isStart":false})]});}
            var Q14;
            {var subQ0=sQuery(id+"F0.wireOp",EDGE,"E5");var subQ1=makeQuery(id+"F0.imprint","IMPRINT",EDGE,{"disambiguationData":[TD([[makeQuery(id+"F0.imprint","INTERSECT",VERTEX,{"derivedFrom":[sQuery(id+"F0.wireOp",EDGE,"E3"),subQ0]}),-1.0]])],"derivedFrom":subQ0});Q14=makeQuery(id+"F2.opChamfer","BLEND_EDGE",EDGE,{"blendedFrom":[makeQuery(id+"F1.opExtrude","CAP_EDGE",EDGE,{"disambiguationData":[OSD([subQ0]),TDD([subQ1])],"isStart":false}),makeQuery(id+"F1.opExtrude","SWEPT_FACE",FACE,{"disambiguationData":[OSD([subQ0]),TDD([subQ1])]})],"blendedInto":[makeQuery(id+"F1.opExtrude","SWEPT_FACE",FACE,{"disambiguationData":[OSD([subQ0]),TDD([subQ1])]})]});}
            var Q15;
            {var subQ0=sQuery(id+"F0.wireOp",EDGE,"E14");var subQ1=sQuery(id+"F0.wireOp",EDGE,"E5");var subQ2=sQuery(id+"F0.wireOp",EDGE,"E3");Q15=makeQuery(id+"F2.opChamfer","BLEND_EDGE",EDGE,{"blendedFrom":[makeQuery(id+"F1.opExtrude","CAP_EDGE",EDGE,{"disambiguationData":[OSD([subQ1]),TDD([makeQuery(id+"F0.imprint","IMPRINT",EDGE,{"disambiguationData":[TD([[makeQuery(id+"F0.imprint","INTERSECT",VERTEX,{"derivedFrom":[subQ2,subQ1]}),-1.0]])],"derivedFrom":subQ1})])],"isStart":false}),makeQuery(id+"F1.opExtrude","CAP_FACE",FACE,{"disambiguationData":[OSD([sQuery(id+"F0.wireOp",EDGE,"E0"),sQuery(id+"F0.wireOp",EDGE,"E1"),sQuery(id+"F0.wireOp",EDGE,"E2"),subQ2,sQuery(id+"F0.wireOp",EDGE,"E4"),subQ1,sQuery(id+"F0.wireOp",EDGE,"E6"),sQuery(id+"F0.wireOp",EDGE,"E7"),sQuery(id+"F0.wireOp",EDGE,"E8"),sQuery(id+"F0.wireOp",EDGE,"E9.bottom"),sQuery(id+"F0.wireOp",EDGE,"E9.left"),sQuery(id+"F0.wireOp",EDGE,"E9.right"),sQuery(id+"F0.wireOp",EDGE,"E12"),subQ0])],"isStart":false})],"blendedInto":[makeQuery(id+"F1.opExtrude","CAP_FACE",FACE,{"disambiguationData":[OSD([sQuery(id+"F0.wireOp",EDGE,"E0"),sQuery(id+"F0.wireOp",EDGE,"E1"),sQuery(id+"F0.wireOp",EDGE,"E2"),subQ2,sQuery(id+"F0.wireOp",EDGE,"E4"),subQ1,sQuery(id+"F0.wireOp",EDGE,"E6"),sQuery(id+"F0.wireOp",EDGE,"E7"),sQuery(id+"F0.wireOp",EDGE,"E8"),sQuery(id+"F0.wireOp",EDGE,"E9.bottom"),sQuery(id+"F0.wireOp",EDGE,"E9.left"),sQuery(id+"F0.wireOp",EDGE,"E9.right"),sQuery(id+"F0.wireOp",EDGE,"E12"),subQ0])],"isStart":false})]});}
            chamfer(context, id + "F10", {"entities" : qUnion([Q0, Q1, Q2, Q3, Q4, Q5, Q6, Q7, Q8, Q9, Q10, Q11, Q12, Q13, Q14, Q15]), "width" : 1.27 * mm, "tangentPropagation" : true});
        }
    });
